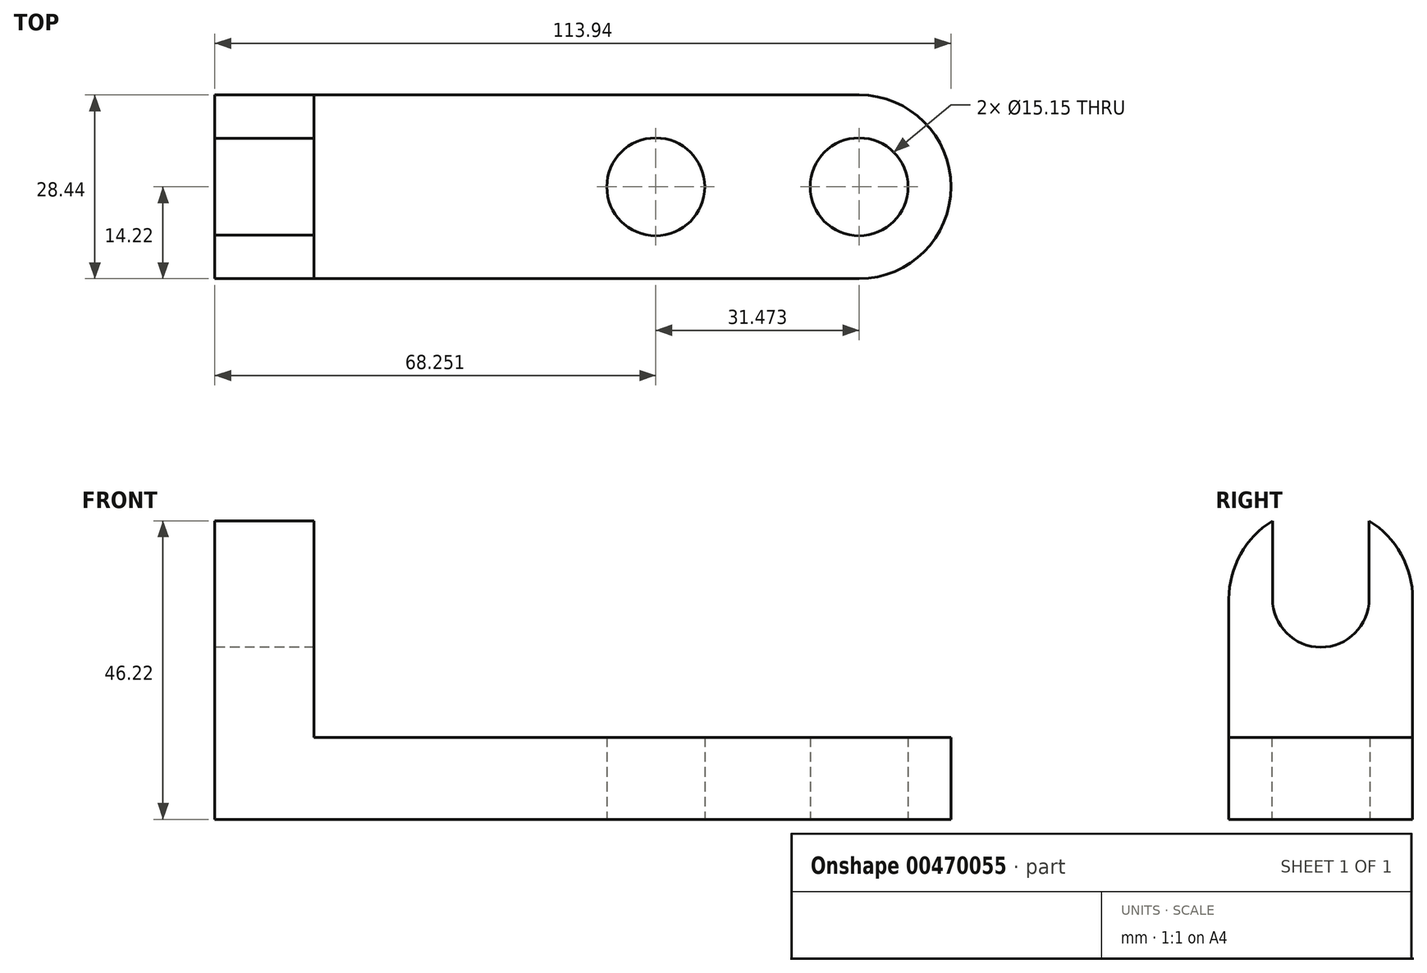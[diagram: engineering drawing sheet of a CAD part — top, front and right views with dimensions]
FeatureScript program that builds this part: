
annotation { "Feature Type Name" : "Feature", "Feature Type Description" : "" }
export const myFeature = defineFeature(function(context is Context, id is Id, definition is map)
    precondition{}
    {
        {
            var Q0;
            Q0=qCreatedBy(makeId("Top.planeOp"),FACE);
            var sketch = newSketch(context, id + "F0", { "sketchPlane" : qUnion([Q0])});
            skLineSegment(sketch, "E0.bottom", {"start": v(49.86, 14.22) * mm, "end": v(-49.86, 14.22) * mm});
            skLineSegment(sketch, "E0.top", {"start": v(49.86, -14.22) * mm, "end": v(-49.86, -14.22) * mm});
            skLineSegment(sketch, "E0.right", {"start": v(-49.86, 14.22) * mm, "end": v(-49.86, -14.22) * mm});
            skPoint(sketch, "E0.middle", {"position": v(0, 0) * mm});
            skArc(sketch, "E1", {"start": v(49.86, 14.22) * mm, "mid": v(64.08, 0) * mm, "end": v(49.86, -14.22) * mm});
            skLineSegment(sketch, "E2", {"start": v(-34.5, 14.22) * mm, "end": v(-34.5, -14.22) * mm});
            skCircle(sketch, "E3", {"center": v(49.86, 0) * mm, "radius": 7.58 * mm});
            skLineSegment(sketch, "E4", {"start": v(49.86, 0) * mm, "end": v(0, 0) * mm, "construction": true});
            skCircle(sketch, "E5", {"center": v(18.4, 0) * mm, "radius": 7.58 * mm});
            skSolve(sketch);
        }
        {
            var Q0;
            Q0 = qSketchRegion(id + "F0", true);
            extrude(context, id + "F1", {"entities" : qUnion([Q0]), "depth" : 12.7 * mm});
        }
        {
            var Q0;
            {var subQ0=sQuery(id+"F0.wireOp",EDGE,"E0.right");Q0=makeQuery(id+"F0.imprint","IMPRINT",FACE,{"disambiguationData":[TD([[makeQuery(id+"F0.imprint","IMPRINT",EDGE,{"derivedFrom":subQ0}),1.0]])]});}
            extrude(context, id + "F2", {"entities" : qUnion([Q0]), "operationType" : NewBodyOperationType.ADD, "depth" : 50.8 * mm});
        }
        {
            var Q0;
            {var subQ0=sQuery(id+"F0.wireOp",EDGE,"E0.right");Q0=makeQuery(id+"F2.boolean.opBoolean","MERGE",FACE,{"derivedFrom":[makeQuery(id+"F1.opExtrude","SWEPT_FACE",FACE,{"disambiguationData":[OSD([subQ0])]}),makeQuery(id+"F2.opExtrude","SWEPT_FACE",FACE,{"disambiguationData":[OSD([subQ0])]})]});}
            var sketch = newSketch(context, id + "F3", { "sketchPlane" : qUnion([Q0])});
            skLineSegment(sketch, "E6", {"start": v(-14.22, 34.13) * mm, "end": v(14.22, 34.13) * mm, "construction": true});
            skArc(sketch, "E7", {"start": v(14.22, 34.13) * mm, "mid": v(12.42, 41.05) * mm, "end": v(7.48, 46.22) * mm});
            skArc(sketch, "E8", {"start": v(-7.48, 34.13) * mm, "mid": v(0, 26.65) * mm, "end": v(7.48, 34.13) * mm});
            skLineSegment(sketch, "E9", {"start": v(-14.22, 34.13) * mm, "end": v(-14.22, 50.8) * mm});
            skLineSegment(sketch, "E10", {"start": v(-14.22, 50.8) * mm, "end": v(14.22, 50.8) * mm});
            skLineSegment(sketch, "E11", {"start": v(14.22, 50.8) * mm, "end": v(14.22, 34.13) * mm});
            skLineSegment(sketch, "E12", {"start": v(-7.48, 34.13) * mm, "end": v(-7.48, 50.8) * mm});
            skLineSegment(sketch, "E13", {"start": v(7.48, 34.13) * mm, "end": v(7.48, 50.8) * mm});
            skLineSegment(sketch, "E14", {"start": v(7.48, 50.8) * mm, "end": v(-7.48, 50.8) * mm});
            skArc(sketch, "E15.trimOffspring", {"start": v(-7.48, 46.22) * mm, "mid": v(-12.42, 41.05) * mm, "end": v(-14.22, 34.13) * mm});
            skSolve(sketch);
        }
        {
            var Q0;
            Q0 = qSketchRegion(id + "F3", true);
            extrude(context, id + "F4", {"entities" : qUnion([Q0]), "operationType" : NewBodyOperationType.REMOVE, "endBound" : BoundingType.THROUGH_ALL, "oppositeDirection" : true, "depth" : 25.4 * mm});
        }
        {
            var Q0;
            Q0 = qSketchRegion(id + "F3", true);
            extrude(context, id + "F5", {"entities" : qUnion([Q0]), "operationType" : NewBodyOperationType.REMOVE, "endBound" : BoundingType.THROUGH_ALL, "oppositeDirection" : true, "depth" : 25.4 * mm});
        }
    });
